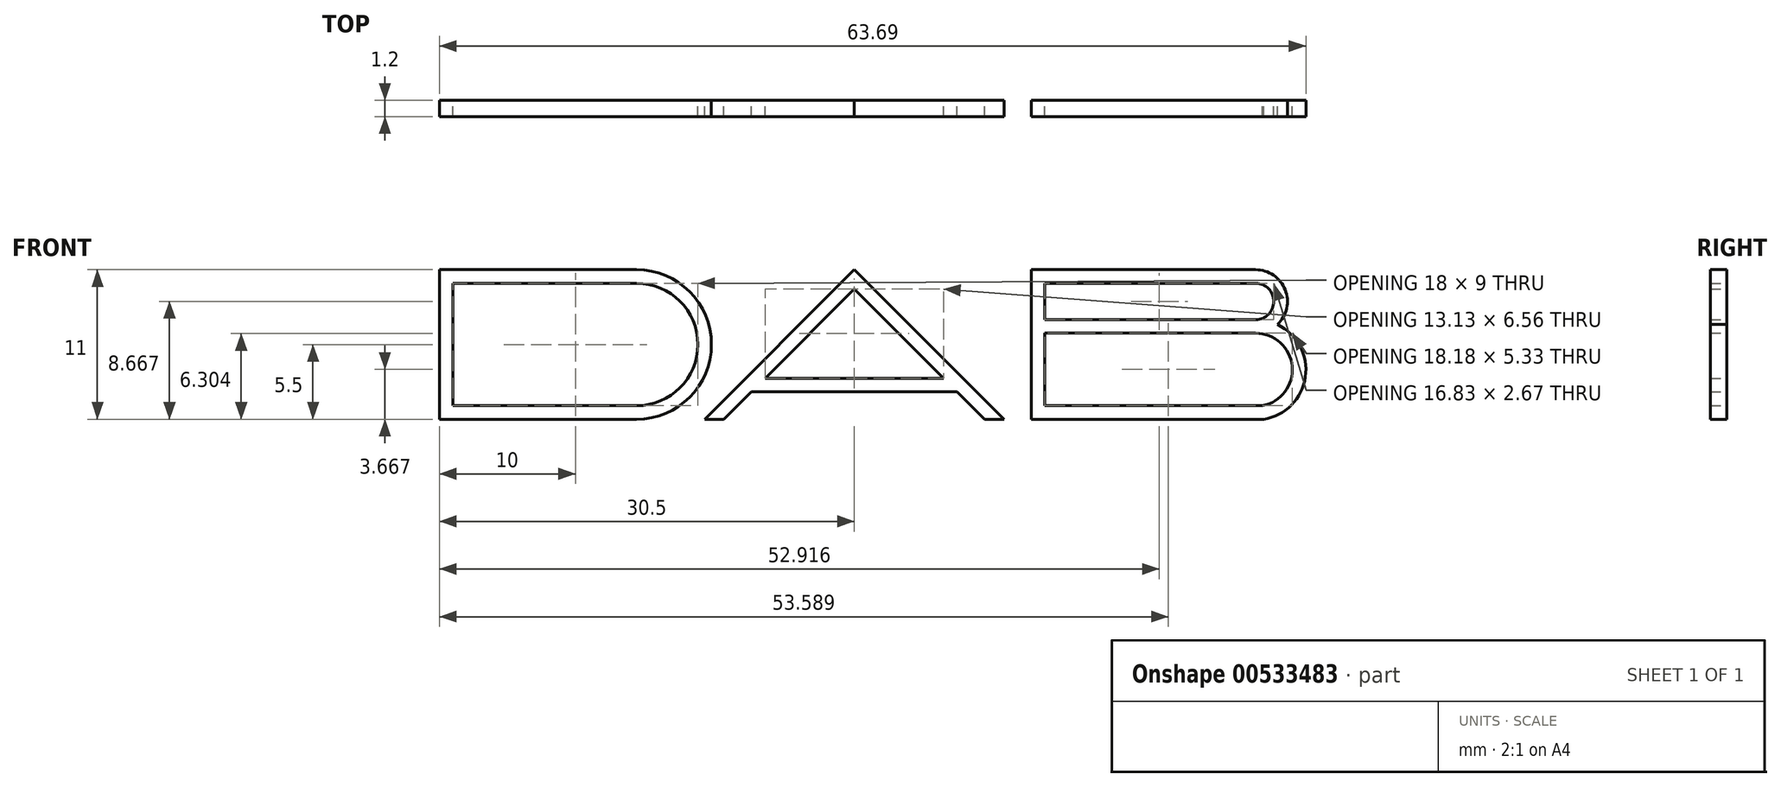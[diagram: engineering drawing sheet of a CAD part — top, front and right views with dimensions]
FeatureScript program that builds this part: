
annotation { "Feature Type Name" : "Feature", "Feature Type Description" : "" }
export const myFeature = defineFeature(function(context is Context, id is Id, definition is map)
    precondition{}
    {
        {
            var Q0;
            Q0=qCreatedBy(makeId("Front.planeOp"),FACE);
            var sketch = newSketch(context, id + "F0", { "sketchPlane" : qUnion([Q0])});
            skLineSegment(sketch, "E0", {"start": v(0, 0) * mm, "end": v(0, 11) * mm});
            skLineSegment(sketch, "E1", {"start": v(0, 11) * mm, "end": v(14.5, 11) * mm});
            skLineSegment(sketch, "E2", {"start": v(0, 0) * mm, "end": v(14.5, 0) * mm});
            skLineSegment(sketch, "E3", {"start": v(19.5, 0) * mm, "end": v(30.5, 11) * mm});
            skLineSegment(sketch, "E4", {"start": v(30.5, 11) * mm, "end": v(41.5, 0) * mm});
            skLineSegment(sketch, "E5", {"start": v(43.5, 0) * mm, "end": v(43.5, 11) * mm});
            skLineSegment(sketch, "E6", {"start": v(43.5, 11) * mm, "end": v(60, 11) * mm});
            skLineSegment(sketch, "E7", {"start": v(43.5, 0) * mm, "end": v(60.58, 0) * mm});
            skArc(sketch, "E8", {"start": v(14.5, 0) * mm, "mid": v(20, 5.5) * mm, "end": v(14.5, 11) * mm});
            skLineSegment(sketch, "E9", {"start": v(19.5, 0) * mm, "end": v(20.91, 0) * mm});
            skLineSegment(sketch, "E10", {"start": v(20.91, 0) * mm, "end": v(22.94, 2.02) * mm});
            skLineSegment(sketch, "E11", {"start": v(30.5, 9.59) * mm, "end": v(37.06, 3.02) * mm});
            skLineSegment(sketch, "E12", {"start": v(40.09, 0) * mm, "end": v(41.5, 0) * mm});
            skLineSegment(sketch, "E13", {"start": v(23.94, 3.02) * mm, "end": v(37.06, 3.02) * mm});
            skLineSegment(sketch, "E14", {"start": v(22.94, 2.02) * mm, "end": v(38.06, 2.02) * mm});
            skLineSegment(sketch, "E15", {"start": v(1, 1) * mm, "end": v(1, 10) * mm});
            skLineSegment(sketch, "E16", {"start": v(1, 10) * mm, "end": v(14.5, 10) * mm});
            skLineSegment(sketch, "E17", {"start": v(1, 1) * mm, "end": v(14.5, 1) * mm});
            skLineSegment(sketch, "E18", {"start": v(44.5, 1) * mm, "end": v(44.5, 6.33) * mm});
            skLineSegment(sketch, "E19", {"start": v(44.5, 10) * mm, "end": v(60, 10) * mm});
            skLineSegment(sketch, "E20", {"start": v(44.5, 1) * mm, "end": v(60.5, 1) * mm});
            skLineSegment(sketch, "E21", {"start": v(44.5, 7.33) * mm, "end": v(60, 7.33) * mm});
            skLineSegment(sketch, "E22", {"start": v(44.5, 6.33) * mm, "end": v(60, 6.33) * mm});
            skLineSegment(sketch, "E23.trimOffspring", {"start": v(44.5, 7.33) * mm, "end": v(44.5, 10) * mm});
            skArc(sketch, "E24", {"start": v(60, 7.33) * mm, "mid": v(61.33, 8.67) * mm, "end": v(60, 10) * mm});
            skArc(sketch, "E25", {"start": v(61.6, 6.97) * mm, "mid": v(62.17, 9.53) * mm, "end": v(60, 11) * mm});
            skArc(sketch, "E26", {"start": v(60.58, 0) * mm, "mid": v(63.65, 3.11) * mm, "end": v(61.6, 6.97) * mm});
            skArc(sketch, "E27", {"start": v(60.5, 1) * mm, "mid": v(62.68, 3.9) * mm, "end": v(60, 6.33) * mm});
            skArc(sketch, "E28", {"start": v(14.5, 1) * mm, "mid": v(19, 5.5) * mm, "end": v(14.5, 10) * mm});
            skLineSegment(sketch, "E29.trimOffspring", {"start": v(23.94, 3.02) * mm, "end": v(30.5, 9.59) * mm});
            skLineSegment(sketch, "E30.trimOffspring", {"start": v(38.06, 2.02) * mm, "end": v(40.09, 0) * mm});
            skSolve(sketch);
        }
        {
            var Q0;
            Q0=makeQuery(id+"F0.imprint","IMPRINT",FACE,{"disambiguationData":[TD([[makeQuery(id+"F0.imprint","IMPRINT",EDGE,{"derivedFrom":sQuery(id+"F0.wireOp",EDGE,"E0")}),-1.0]])]});
            var Q1;
            Q1=makeQuery(id+"F0.imprint","IMPRINT",FACE,{"disambiguationData":[TD([[makeQuery(id+"F0.imprint","IMPRINT",EDGE,{"derivedFrom":sQuery(id+"F0.wireOp",EDGE,"E3")}),-1.0]])]});
            var Q2;
            Q2=makeQuery(id+"F0.imprint","IMPRINT",FACE,{"disambiguationData":[TD([[makeQuery(id+"F0.imprint","IMPRINT",EDGE,{"derivedFrom":sQuery(id+"F0.wireOp",EDGE,"E5")}),-1.0]])]});
            extrude(context, id + "F1", {"entities" : qUnion([Q0, Q1, Q2]), "depth" : 1.2 * mm, "offsetDistance" : 25 * mm});
        }
    });
